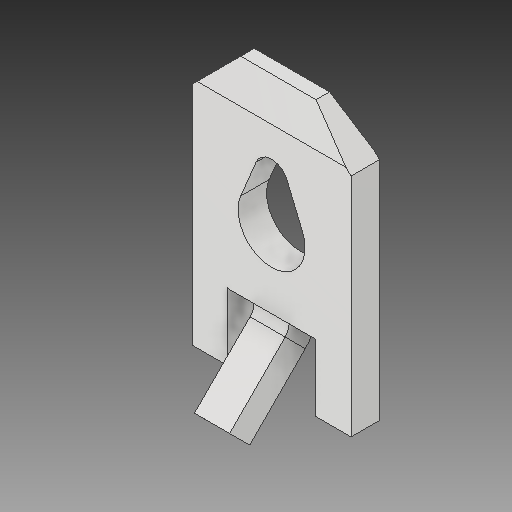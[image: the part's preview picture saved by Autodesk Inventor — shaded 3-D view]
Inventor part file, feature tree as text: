
AUTODESK INVENTOR PART (.ipt)
format: ipt  version: 2019.4 (Build 234330000, 330)  size: 112,640 bytes
history: native  units: mm
features: sketch x1
ambient origin geometry x8: Origin, YZ Plane, XZ Plane, XY Plane, X Axis, Y Axis, Z Axis, Center Point
bodies: Solid1 (feature_tree)
feature tree (1):
  sketch  "Sketched Bend1"
